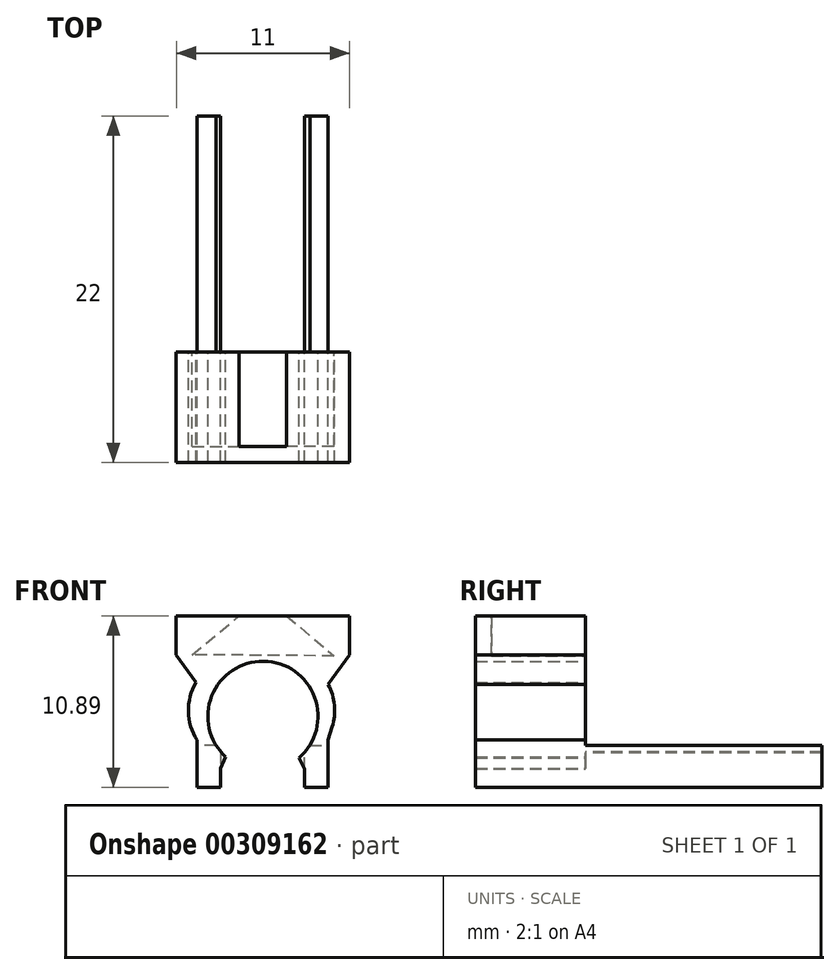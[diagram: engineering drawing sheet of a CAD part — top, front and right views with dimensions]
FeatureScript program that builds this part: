
annotation { "Feature Type Name" : "Feature", "Feature Type Description" : "" }
export const myFeature = defineFeature(function(context is Context, id is Id, definition is map)
    precondition{}
    {
        {
            var Q0;
            Q0=qCreatedBy(makeId("Front.planeOp"),FACE);
            var sketch = newSketch(context, id + "F0", { "sketchPlane" : qUnion([Q0])});
            skLineSegment(sketch, "E0", {"start": v(-3.34, -1.59) * mm, "end": v(-3.32, -1.6) * mm});
            skLineSegment(sketch, "E1", {"start": v(-3.32, -1.6) * mm, "end": v(-3.32, -2.3) * mm});
            skLineSegment(sketch, "E2", {"start": v(-3.32, -4.96) * mm, "end": v(-2.6, -4.96) * mm});
            skLineSegment(sketch, "E3", {"start": v(3.45, -1.64) * mm, "end": v(3.45, -2.3) * mm});
            skLineSegment(sketch, "E4", {"start": v(-4.1, -1.95) * mm, "end": v(-4.1, -4.96) * mm});
            skLineSegment(sketch, "E5", {"start": v(-4.1, -4.96) * mm, "end": v(-3.32, -4.96) * mm});
            skLineSegment(sketch, "E6.MirrorCS", {"start": v(4.22, -1.95) * mm, "end": v(4.22, -4.96) * mm});
            skLineSegment(sketch, "E7", {"start": v(-4.1, -1.95) * mm, "end": v(-3.32, -1.6) * mm});
            skLineSegment(sketch, "E8", {"start": v(4.22, -1.95) * mm, "end": v(3.45, -1.64) * mm});
            skLineSegment(sketch, "E9", {"start": v(0.1, 3.43) * mm, "end": v(-4.4, 3.47) * mm});
            skLineSegment(sketch, "E10", {"start": v(0.1, 3.43) * mm, "end": v(4.6, 3.4) * mm});
            skLineSegment(sketch, "E11", {"start": v(0.1, 3.43) * mm, "end": v(0.1, 5.93) * mm, "construction": true});
            skLineSegment(sketch, "E12", {"start": v(-4.4, 3.47) * mm, "end": v(-1.41, 5.93) * mm});
            skLineSegment(sketch, "E13", {"start": v(1.6, 5.93) * mm, "end": v(4.6, 3.4) * mm});
            skLineSegment(sketch, "E14", {"start": v(-1.41, 5.93) * mm, "end": v(-5.41, 5.93) * mm});
            skLineSegment(sketch, "E15", {"start": v(-5.41, 5.93) * mm, "end": v(-5.41, 3.47) * mm});
            skLineSegment(sketch, "E16", {"start": v(-5.41, 3.47) * mm, "end": v(-4.17, 1.7) * mm});
            skLineSegment(sketch, "E17", {"start": v(1.6, 5.93) * mm, "end": v(5.59, 5.93) * mm});
            skLineSegment(sketch, "E18", {"start": v(5.59, 5.93) * mm, "end": v(5.59, 3.47) * mm});
            skLineSegment(sketch, "E19", {"start": v(5.59, 3.47) * mm, "end": v(4.23, 1.59) * mm});
            skLineSegment(sketch, "E20", {"start": v(-1.41, 5.93) * mm, "end": v(1.6, 5.93) * mm});
            skLineSegment(sketch, "E21", {"start": v(-3.32, -2.3) * mm, "end": v(-4.1, -2.3) * mm});
            skLineSegment(sketch, "E22", {"start": v(3.45, -2.3) * mm, "end": v(4.22, -2.3) * mm});
            skLineSegment(sketch, "E23", {"start": v(3.45, -2.3) * mm, "end": v(3.45, -4.96) * mm, "construction": true});
            skLineSegment(sketch, "E24.0", {"start": v(2.72, -3.79) * mm, "end": v(2.72, -4.96) * mm});
            skLineSegment(sketch, "E25.0", {"start": v(-2.6, -2.7) * mm, "end": v(-2.6, -4.96) * mm});
            skLineSegment(sketch, "E26", {"start": v(-2.88, -2.3) * mm, "end": v(-3.32, -2.3) * mm});
            skPoint(sketch, "E27.orphan", {"position": v(2.25, -2.28) * mm});
            skPoint(sketch, "E28.orphan", {"position": v(-2.12, -2.28) * mm});
            skLineSegment(sketch, "E29", {"start": v(2.72, -3.79) * mm, "end": v(2.4, -3.08) * mm});
            skLineSegment(sketch, "E30", {"start": v(-2.28, -3.02) * mm, "end": v(-2.6, -3.74) * mm});
            skLineSegment(sketch, "E31", {"start": v(3.45, -2.3) * mm, "end": v(3.07, -2.3) * mm});
            skLineSegment(sketch, "E32", {"start": v(2.72, -3.79) * mm, "end": v(2.72, -2.76) * mm});
            skLineSegment(sketch, "E33", {"start": v(2.72, -4.96) * mm, "end": v(4.22, -4.95) * mm});
            skArc(sketch, "E34", {"start": v(2.4, -3.08) * mm, "mid": v(0.14, 3.05) * mm, "end": v(-2.28, -3.02) * mm});
            skArc(sketch, "E35", {"start": v(-4.17, 1.7) * mm, "mid": v(-4.64, -0.14) * mm, "end": v(-4.1, -1.95) * mm});
            skArc(sketch, "E36.MirrorCS", {"start": v(4.23, 1.59) * mm, "mid": v(4.63, 0.26) * mm, "end": v(4.48, -1.12) * mm});
            skPoint(sketch, "E37.orphan", {"position": v(-3.48, 0.71) * mm});
            skPoint(sketch, "E38.orphan", {"position": v(3.6, 0.71) * mm});
            skPoint(sketch, "E39.orphan", {"position": v(4.17, 1.7) * mm});
            skPoint(sketch, "E40.orphan", {"position": v(4.1, -1.95) * mm});
            skLineSegment(sketch, "E41", {"start": v(4.22, -1.95) * mm, "end": v(4.48, -1.12) * mm});
            skSolve(sketch);
        }
        {
            var Q0;
            Q0=qSketchRegion(id+"F0",true);
            extrude(context, id + "F1", {"entities" : qUnion([Q0]), "depth" : 7 * mm});
        }
        {
            var Q0;
            Q0=makeQuery(id+"F0.imprint","IMPRINT",FACE,{"disambiguationData":[TD([[makeQuery(id+"F0.imprint","IMPRINT",EDGE,{"derivedFrom":sQuery(id+"F0.wireOp",EDGE,"E9")}),-1.0]])]});
            extrude(context, id + "F2", {"entities" : qUnion([Q0]), "operationType" : NewBodyOperationType.REMOVE, "depth" : 6 * mm});
        }
        {
            var Q0;
            Q0=makeQuery(id+"F0.imprint","IMPRINT",FACE,{"disambiguationData":[TD([[makeQuery(id+"F0.imprint","IMPRINT",EDGE,{"derivedFrom":sQuery(id+"F0.wireOp",EDGE,"f47f5537-e82d-4f6e-b3b4-383c7a984791")}),-1.0]])]});
            var Q1;
            Q1=makeQuery(id+"F0.imprint","IMPRINT",FACE,{"disambiguationData":[TD([[makeQuery(id+"F0.imprint","IMPRINT",EDGE,{"derivedFrom":sQuery(id+"F0.wireOp",EDGE,"E2")}),1.0]])]});
            var Q2;
            {var subQ0=sQuery(id+"F0.wireOp",EDGE,"E22");Q2=makeQuery(id+"F0.imprint","IMPRINT",FACE,{"disambiguationData":[TD([[makeQuery(id+"F0.imprint","IMPRINT",EDGE,{"derivedFrom":subQ0}),-1.0]])]});}
            extrude(context, id + "F3", {"entities" : qUnion([Q0, Q1, Q2]), "operationType" : NewBodyOperationType.ADD, "oppositeDirection" : true, "depth" : 15 * mm, "offsetDistance" : 25 * mm});
        }
    });
